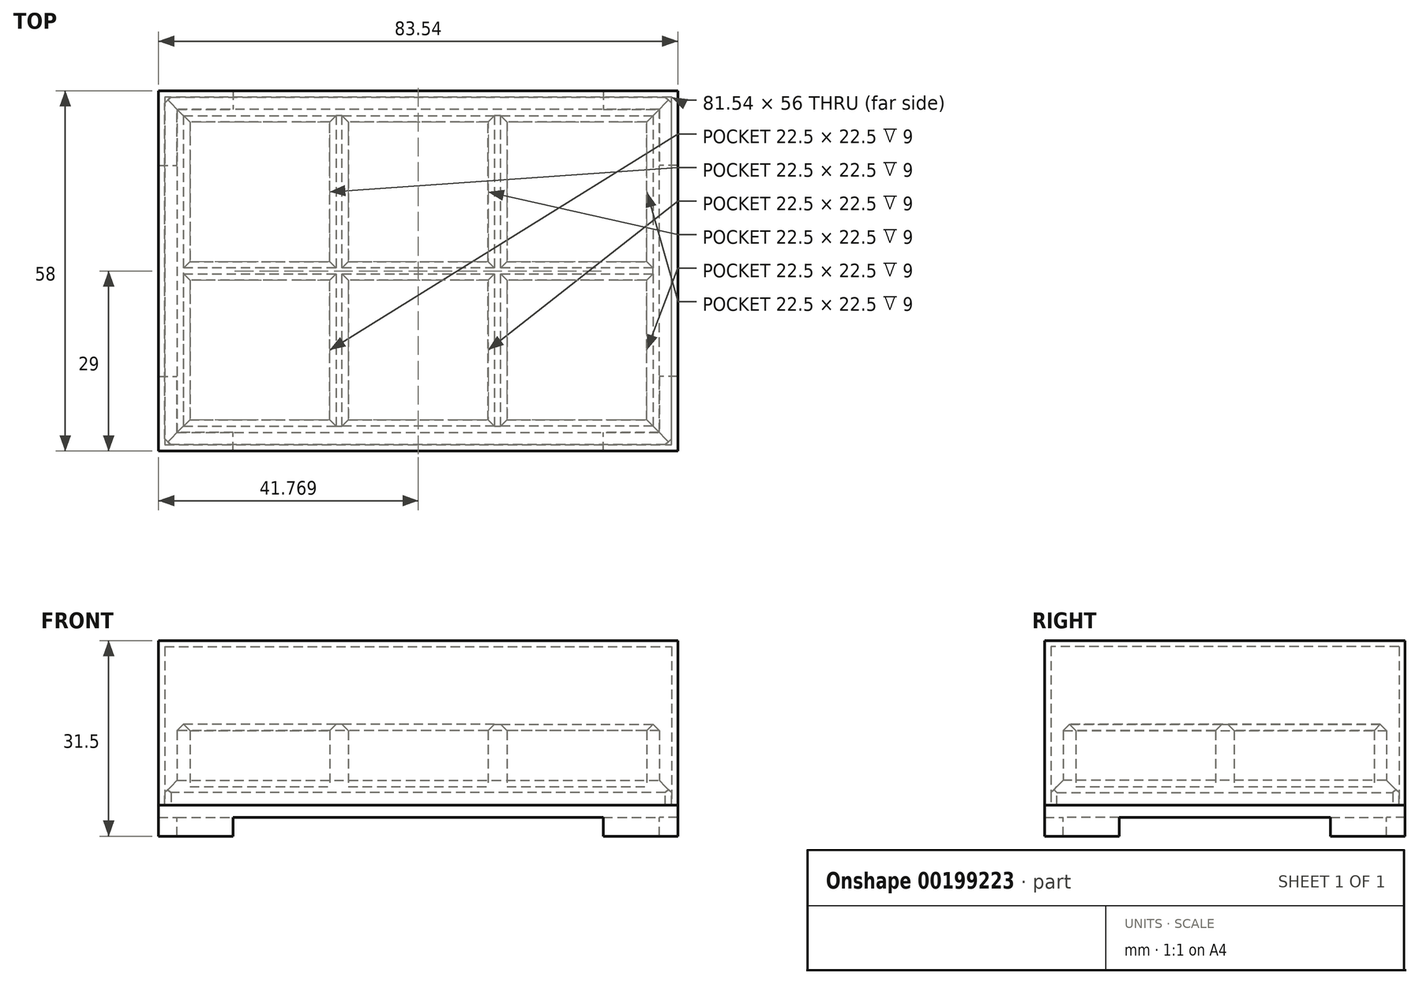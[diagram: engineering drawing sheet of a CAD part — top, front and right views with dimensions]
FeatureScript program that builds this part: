
annotation { "Feature Type Name" : "Feature", "Feature Type Description" : "" }
export const myFeature = defineFeature(function(context is Context, id is Id, definition is map)
    precondition{}
    {
        {
            var Q0;
            Q0=qCreatedBy(makeId("Top.planeOp"),FACE);
            var sketch = newSketch(context, id + "F0", { "sketchPlane" : qUnion([Q0])});
            skLineSegment(sketch, "E0.bottom", {"start": v(0, 0) * mm, "end": v(22.5, 0) * mm});
            skLineSegment(sketch, "E0.top", {"start": v(0, 22.5) * mm, "end": v(22.5, 22.5) * mm});
            skLineSegment(sketch, "E0.left", {"start": v(0, 0) * mm, "end": v(0, 22.5) * mm});
            skLineSegment(sketch, "E0.right", {"start": v(22.5, 0) * mm, "end": v(22.5, 22.5) * mm});
            skLineSegment(sketch, "E1.0.1.0", {"start": v(0, 48) * mm, "end": v(22.5, 48) * mm});
            skLineSegment(sketch, "E1.0.1.1", {"start": v(0, 25.5) * mm, "end": v(0, 48) * mm});
            skLineSegment(sketch, "E1.0.1.2", {"start": v(0, 25.5) * mm, "end": v(22.5, 25.5) * mm});
            skLineSegment(sketch, "E1.0.1.3", {"start": v(22.5, 25.5) * mm, "end": v(22.5, 48) * mm});
            skLineSegment(sketch, "E1.1.0.0", {"start": v(25.5, 22.5) * mm, "end": v(48, 22.5) * mm});
            skLineSegment(sketch, "E1.1.0.1", {"start": v(25.5, 0) * mm, "end": v(25.5, 22.5) * mm});
            skLineSegment(sketch, "E1.1.0.2", {"start": v(25.5, 0) * mm, "end": v(48, 0) * mm});
            skLineSegment(sketch, "E1.1.0.3", {"start": v(48, 0) * mm, "end": v(48, 22.5) * mm});
            skLineSegment(sketch, "E1.1.1.0", {"start": v(25.5, 48) * mm, "end": v(48, 48) * mm});
            skLineSegment(sketch, "E1.1.1.1", {"start": v(25.5, 25.5) * mm, "end": v(25.5, 48) * mm});
            skLineSegment(sketch, "E1.1.1.2", {"start": v(25.5, 25.5) * mm, "end": v(48, 25.5) * mm});
            skLineSegment(sketch, "E1.1.1.3", {"start": v(48, 25.5) * mm, "end": v(48, 48) * mm});
            skLineSegment(sketch, "E1.2.0.0", {"start": v(51, 22.5) * mm, "end": v(73.5, 22.5) * mm});
            skLineSegment(sketch, "E1.2.0.1", {"start": v(51, 0) * mm, "end": v(51, 22.5) * mm});
            skLineSegment(sketch, "E1.2.0.2", {"start": v(51, 0) * mm, "end": v(73.5, 0) * mm});
            skLineSegment(sketch, "E1.2.0.3", {"start": v(73.5, 0) * mm, "end": v(73.5, 22.5) * mm});
            skLineSegment(sketch, "E1.2.1.0", {"start": v(51, 48) * mm, "end": v(73.5, 48) * mm});
            skLineSegment(sketch, "E1.2.1.1", {"start": v(51, 25.5) * mm, "end": v(51, 48) * mm});
            skLineSegment(sketch, "E1.2.1.2", {"start": v(51, 25.5) * mm, "end": v(73.5, 25.5) * mm});
            skLineSegment(sketch, "E1.2.1.3", {"start": v(73.5, 25.5) * mm, "end": v(73.5, 48) * mm});
            skLineSegment(sketch, "E1.direction1", {"start": v(0, 22.5) * mm, "end": v(25.5, 22.5) * mm, "construction": true});
            skLineSegment(sketch, "E1.direction2", {"start": v(0, 22.5) * mm, "end": v(0, 48) * mm, "construction": true});
            skLineSegment(sketch, "E2.bottom", {"start": v(-2.04, -2) * mm, "end": v(75.5, -2) * mm});
            skLineSegment(sketch, "E2.top", {"start": v(-2.04, 50) * mm, "end": v(75.5, 50) * mm});
            skLineSegment(sketch, "E2.left", {"start": v(-2.04, -2) * mm, "end": v(-2.04, 50) * mm});
            skLineSegment(sketch, "E2.right", {"start": v(75.5, -2) * mm, "end": v(75.5, 50) * mm});
            skSolve(sketch);
        }
        {
            var Q0;
            Q0 = qSketchRegion(id + "F0", true);
            extrude(context, id + "F1", {"entities" : qUnion([Q0]), "depth" : 10 * mm});
        }
        {
            var Q0;
            Q0=makeQuery(id+"F1.opExtrude","CAP_FACE",FACE,{"disambiguationData":[OSD([sQuery(id+"F0.wireOp",EDGE,"E0.bottom"),sQuery(id+"F0.wireOp",EDGE,"E0.top"),sQuery(id+"F0.wireOp",EDGE,"E0.left"),sQuery(id+"F0.wireOp",EDGE,"E0.right"),sQuery(id+"F0.wireOp",EDGE,"E1.0.1.0"),sQuery(id+"F0.wireOp",EDGE,"E1.0.1.1"),sQuery(id+"F0.wireOp",EDGE,"E1.0.1.2"),sQuery(id+"F0.wireOp",EDGE,"E1.0.1.3"),sQuery(id+"F0.wireOp",EDGE,"E1.1.0.0"),sQuery(id+"F0.wireOp",EDGE,"E1.1.0.1"),sQuery(id+"F0.wireOp",EDGE,"E1.1.0.2"),sQuery(id+"F0.wireOp",EDGE,"E1.1.0.3"),sQuery(id+"F0.wireOp",EDGE,"E1.1.1.0"),sQuery(id+"F0.wireOp",EDGE,"E1.1.1.1"),sQuery(id+"F0.wireOp",EDGE,"E1.1.1.2"),sQuery(id+"F0.wireOp",EDGE,"E1.1.1.3"),sQuery(id+"F0.wireOp",EDGE,"E1.2.0.0"),sQuery(id+"F0.wireOp",EDGE,"E1.2.0.1"),sQuery(id+"F0.wireOp",EDGE,"E1.2.0.2"),sQuery(id+"F0.wireOp",EDGE,"E1.2.0.3"),sQuery(id+"F0.wireOp",EDGE,"E1.2.1.0"),sQuery(id+"F0.wireOp",EDGE,"E1.2.1.1"),sQuery(id+"F0.wireOp",EDGE,"E1.2.1.2"),sQuery(id+"F0.wireOp",EDGE,"E1.2.1.3"),sQuery(id+"F0.wireOp",EDGE,"E2.bottom"),sQuery(id+"F0.wireOp",EDGE,"E2.top"),sQuery(id+"F0.wireOp",EDGE,"E2.left"),sQuery(id+"F0.wireOp",EDGE,"E2.right")])],"isStart":true});
            var sketch = newSketch(context, id + "F2", { "sketchPlane" : qUnion([Q0])});
            skLineSegment(sketch, "E3.0", {"start": v(-4.04, 4) * mm, "end": v(-4.04, -52) * mm});
            skLineSegment(sketch, "E3.1", {"start": v(-4.04, 4) * mm, "end": v(77.5, 4) * mm});
            skLineSegment(sketch, "E3.2", {"start": v(77.5, 4) * mm, "end": v(77.5, -52) * mm});
            skLineSegment(sketch, "E3.3", {"start": v(-4.04, -52) * mm, "end": v(77.5, -52) * mm});
            skSolve(sketch);
        }
        {
            var Q0;
            Q0 = qSketchRegion(id + "F2", true);
            extrude(context, id + "F3", {"entities" : qUnion([Q0]), "operationType" : NewBodyOperationType.ADD, "depth" : 3 * mm});
        }
        {
            var Q0;
            Q0=makeQuery(id+"F3.opExtrude","CAP_FACE",FACE,{"disambiguationData":[OSD([sQuery(id+"F2.wireOp",EDGE,"E3.0"),sQuery(id+"F2.wireOp",EDGE,"E3.1"),sQuery(id+"F2.wireOp",EDGE,"E3.2"),sQuery(id+"F2.wireOp",EDGE,"E3.3")])],"isStart":false});
            var sketch = newSketch(context, id + "F4", { "sketchPlane" : qUnion([Q0])});
            skLineSegment(sketch, "E4.0", {"start": v(78.5, 5) * mm, "end": v(-5.04, 5) * mm});
            skLineSegment(sketch, "E4.1", {"start": v(78.5, -53) * mm, "end": v(78.5, 5) * mm});
            skLineSegment(sketch, "E4.2", {"start": v(-5.04, -53) * mm, "end": v(78.5, -53) * mm});
            skLineSegment(sketch, "E4.3", {"start": v(-5.04, 5) * mm, "end": v(-5.04, -53) * mm});
            skSolve(sketch);
        }
        {
            var Q0;
            Q0 = qSketchRegion(id + "F4", true);
            extrude(context, id + "F5", {"entities" : qUnion([Q0]), "operationType" : NewBodyOperationType.ADD, "depth" : 2 * mm});
        }
        {
            var Q0;
            Q0=makeQuery(id+"F3.opExtrude","CAP_EDGE",EDGE,{"disambiguationData":[OSD([sQuery(id+"F2.wireOp",EDGE,"E3.2")])],"isStart":true});
            var Q1;
            Q1=makeQuery(id+"F3.opExtrude","CAP_EDGE",EDGE,{"disambiguationData":[OSD([sQuery(id+"F2.wireOp",EDGE,"E3.3")])],"isStart":true});
            var Q2;
            Q2=makeQuery(id+"F3.opExtrude","CAP_EDGE",EDGE,{"disambiguationData":[OSD([sQuery(id+"F2.wireOp",EDGE,"E3.0")])],"isStart":true});
            var Q3;
            Q3=makeQuery(id+"F3.opExtrude","CAP_EDGE",EDGE,{"disambiguationData":[OSD([sQuery(id+"F2.wireOp",EDGE,"E3.1")])],"isStart":true});
            chamfer(context, id + "F6", {"entities" : qUnion([Q0, Q1, Q2, Q3]), "width" : 1 * mm, "tangentPropagation" : true});
        }
        {
            var Q0;
            Q0=makeQuery(id+"F1.opExtrude","CAP_EDGE",EDGE,{"disambiguationData":[OSD([sQuery(id+"F0.wireOp",EDGE,"E0.right")])],"isStart":false});
            var Q1;
            Q1=makeQuery(id+"F1.opExtrude","CAP_EDGE",EDGE,{"disambiguationData":[OSD([sQuery(id+"F0.wireOp",EDGE,"E0.bottom")])],"isStart":false});
            var Q2;
            Q2=makeQuery(id+"F1.opExtrude","CAP_EDGE",EDGE,{"disambiguationData":[OSD([sQuery(id+"F0.wireOp",EDGE,"E0.left")])],"isStart":false});
            var Q3;
            Q3=makeQuery(id+"F1.opExtrude","CAP_EDGE",EDGE,{"disambiguationData":[OSD([sQuery(id+"F0.wireOp",EDGE,"E0.top")])],"isStart":false});
            var Q4;
            Q4=makeQuery(id+"F1.opExtrude","CAP_EDGE",EDGE,{"disambiguationData":[OSD([sQuery(id+"F0.wireOp",EDGE,"E1.1.0.3")])],"isStart":false});
            var Q5;
            Q5=makeQuery(id+"F1.opExtrude","CAP_EDGE",EDGE,{"disambiguationData":[OSD([sQuery(id+"F0.wireOp",EDGE,"E1.1.0.2")])],"isStart":false});
            var Q6;
            Q6=makeQuery(id+"F1.opExtrude","CAP_EDGE",EDGE,{"disambiguationData":[OSD([sQuery(id+"F0.wireOp",EDGE,"E1.1.0.1")])],"isStart":false});
            var Q7;
            Q7=makeQuery(id+"F1.opExtrude","CAP_EDGE",EDGE,{"disambiguationData":[OSD([sQuery(id+"F0.wireOp",EDGE,"E1.1.0.0")])],"isStart":false});
            var Q8;
            Q8=makeQuery(id+"F1.opExtrude","CAP_EDGE",EDGE,{"disambiguationData":[OSD([sQuery(id+"F0.wireOp",EDGE,"E1.2.0.0")])],"isStart":false});
            var Q9;
            Q9=makeQuery(id+"F1.opExtrude","CAP_EDGE",EDGE,{"disambiguationData":[OSD([sQuery(id+"F0.wireOp",EDGE,"E1.2.0.3")])],"isStart":false});
            var Q10;
            Q10=makeQuery(id+"F1.opExtrude","CAP_EDGE",EDGE,{"disambiguationData":[OSD([sQuery(id+"F0.wireOp",EDGE,"E1.2.0.2")])],"isStart":false});
            var Q11;
            Q11=makeQuery(id+"F1.opExtrude","CAP_EDGE",EDGE,{"disambiguationData":[OSD([sQuery(id+"F0.wireOp",EDGE,"E1.2.0.1")])],"isStart":false});
            var Q12;
            Q12=makeQuery(id+"F1.opExtrude","CAP_EDGE",EDGE,{"disambiguationData":[OSD([sQuery(id+"F0.wireOp",EDGE,"E1.2.1.2")])],"isStart":false});
            var Q13;
            Q13=makeQuery(id+"F1.opExtrude","CAP_EDGE",EDGE,{"disambiguationData":[OSD([sQuery(id+"F0.wireOp",EDGE,"E1.2.1.3")])],"isStart":false});
            var Q14;
            Q14=makeQuery(id+"F1.opExtrude","CAP_EDGE",EDGE,{"disambiguationData":[OSD([sQuery(id+"F0.wireOp",EDGE,"E1.2.1.0")])],"isStart":false});
            var Q15;
            Q15=makeQuery(id+"F1.opExtrude","CAP_EDGE",EDGE,{"disambiguationData":[OSD([sQuery(id+"F0.wireOp",EDGE,"E1.2.1.1")])],"isStart":false});
            var Q16;
            Q16=makeQuery(id+"F1.opExtrude","CAP_EDGE",EDGE,{"disambiguationData":[OSD([sQuery(id+"F0.wireOp",EDGE,"E1.1.1.2")])],"isStart":false});
            var Q17;
            Q17=makeQuery(id+"F1.opExtrude","CAP_EDGE",EDGE,{"disambiguationData":[OSD([sQuery(id+"F0.wireOp",EDGE,"E1.1.1.3")])],"isStart":false});
            var Q18;
            Q18=makeQuery(id+"F1.opExtrude","CAP_EDGE",EDGE,{"disambiguationData":[OSD([sQuery(id+"F0.wireOp",EDGE,"E1.1.1.0")])],"isStart":false});
            var Q19;
            Q19=makeQuery(id+"F1.opExtrude","CAP_EDGE",EDGE,{"disambiguationData":[OSD([sQuery(id+"F0.wireOp",EDGE,"E1.0.1.3")])],"isStart":false});
            var Q20;
            Q20=makeQuery(id+"F1.opExtrude","CAP_EDGE",EDGE,{"disambiguationData":[OSD([sQuery(id+"F0.wireOp",EDGE,"E1.0.1.2")])],"isStart":false});
            var Q21;
            Q21=makeQuery(id+"F1.opExtrude","CAP_EDGE",EDGE,{"disambiguationData":[OSD([sQuery(id+"F0.wireOp",EDGE,"E1.0.1.1")])],"isStart":false});
            var Q22;
            Q22=makeQuery(id+"F1.opExtrude","CAP_FACE",FACE,{"disambiguationData":[OSD([sQuery(id+"F0.wireOp",EDGE,"E0.bottom"),sQuery(id+"F0.wireOp",EDGE,"E0.top"),sQuery(id+"F0.wireOp",EDGE,"E0.left"),sQuery(id+"F0.wireOp",EDGE,"E0.right"),sQuery(id+"F0.wireOp",EDGE,"E1.0.1.0"),sQuery(id+"F0.wireOp",EDGE,"E1.0.1.1"),sQuery(id+"F0.wireOp",EDGE,"E1.0.1.2"),sQuery(id+"F0.wireOp",EDGE,"E1.0.1.3"),sQuery(id+"F0.wireOp",EDGE,"E1.1.0.0"),sQuery(id+"F0.wireOp",EDGE,"E1.1.0.1"),sQuery(id+"F0.wireOp",EDGE,"E1.1.0.2"),sQuery(id+"F0.wireOp",EDGE,"E1.1.0.3"),sQuery(id+"F0.wireOp",EDGE,"E1.1.1.0"),sQuery(id+"F0.wireOp",EDGE,"E1.1.1.1"),sQuery(id+"F0.wireOp",EDGE,"E1.1.1.2"),sQuery(id+"F0.wireOp",EDGE,"E1.1.1.3"),sQuery(id+"F0.wireOp",EDGE,"E1.2.0.0"),sQuery(id+"F0.wireOp",EDGE,"E1.2.0.1"),sQuery(id+"F0.wireOp",EDGE,"E1.2.0.2"),sQuery(id+"F0.wireOp",EDGE,"E1.2.0.3"),sQuery(id+"F0.wireOp",EDGE,"E1.2.1.0"),sQuery(id+"F0.wireOp",EDGE,"E1.2.1.1"),sQuery(id+"F0.wireOp",EDGE,"E1.2.1.2"),sQuery(id+"F0.wireOp",EDGE,"E1.2.1.3"),sQuery(id+"F0.wireOp",EDGE,"E2.bottom"),sQuery(id+"F0.wireOp",EDGE,"E2.top"),sQuery(id+"F0.wireOp",EDGE,"E2.left"),sQuery(id+"F0.wireOp",EDGE,"E2.right")])],"isStart":false});
            var Q23;
            Q23=makeQuery(id+"F1.opExtrude","CAP_EDGE",EDGE,{"disambiguationData":[OSD([sQuery(id+"F0.wireOp",EDGE,"E2.top")])],"isStart":true});
            var Q24;
            Q24=makeQuery(id+"F1.opExtrude","CAP_EDGE",EDGE,{"disambiguationData":[OSD([sQuery(id+"F0.wireOp",EDGE,"E2.left")])],"isStart":true});
            var Q25;
            Q25=makeQuery(id+"F1.opExtrude","CAP_EDGE",EDGE,{"disambiguationData":[OSD([sQuery(id+"F0.wireOp",EDGE,"E2.right")])],"isStart":true});
            var Q26;
            Q26=makeQuery(id+"F1.opExtrude","CAP_EDGE",EDGE,{"disambiguationData":[OSD([sQuery(id+"F0.wireOp",EDGE,"E2.bottom")])],"isStart":true});
            var Q27;
            Q27=makeQuery(id+"F3.opExtrude","SWEPT_EDGE",EDGE,{"disambiguationData":[OSD([sQuery(id+"F2.wireOp",EDGE,"E3.0"),sQuery(id+"F2.wireOp",EDGE,"E3.1")])]});
            var Q28;
            Q28=makeQuery(id+"F3.opExtrude","SWEPT_EDGE",EDGE,{"disambiguationData":[OSD([sQuery(id+"F2.wireOp",EDGE,"E3.0"),sQuery(id+"F2.wireOp",EDGE,"E3.3")])]});
            var Q29;
            Q29=makeQuery(id+"F3.opExtrude","SWEPT_EDGE",EDGE,{"disambiguationData":[OSD([sQuery(id+"F2.wireOp",EDGE,"E3.2"),sQuery(id+"F2.wireOp",EDGE,"E3.3")])]});
            var Q30;
            Q30=makeQuery(id+"F3.opExtrude","SWEPT_EDGE",EDGE,{"disambiguationData":[OSD([sQuery(id+"F2.wireOp",EDGE,"E3.1"),sQuery(id+"F2.wireOp",EDGE,"E3.2")])]});
            chamfer(context, id + "F7", {"entities" : qUnion([Q0, Q1, Q2, Q3, Q4, Q5, Q6, Q7, Q8, Q9, Q10, Q11, Q12, Q13, Q14, Q15, Q16, Q17, Q18, Q19, Q20, Q21, Q22, Q23, Q24, Q25, Q26, Q27, Q28, Q29, Q30]), "width" : 1 * mm, "tangentPropagation" : true});
        }
        {
            var Q0;
            Q0=makeQuery(id+"F5.opExtrude","CAP_FACE",FACE,{"disambiguationData":[OSD([sQuery(id+"F4.wireOp",EDGE,"E4.0"),sQuery(id+"F4.wireOp",EDGE,"E4.1"),sQuery(id+"F4.wireOp",EDGE,"E4.2"),sQuery(id+"F4.wireOp",EDGE,"E4.3")])],"isStart":false});
            var sketch = newSketch(context, id + "F8", { "sketchPlane" : qUnion([Q0])});
            skLineSegment(sketch, "E5.0.0", {"start": v(78.5, -53) * mm, "end": v(78.5, 5) * mm});
            skLineSegment(sketch, "E5.0.1", {"start": v(78.5, 5) * mm, "end": v(-5.04, 5) * mm});
            skLineSegment(sketch, "E5.0.2", {"start": v(-5.04, 5) * mm, "end": v(-5.04, -53) * mm});
            skLineSegment(sketch, "E5.0.3", {"start": v(-5.04, -53) * mm, "end": v(78.5, -53) * mm});
            skLineSegment(sketch, "E6.0", {"start": v(75.5, -50) * mm, "end": v(75.5, 2) * mm});
            skLineSegment(sketch, "E6.1", {"start": v(-2.04, -50) * mm, "end": v(75.5, -50) * mm});
            skLineSegment(sketch, "E6.2", {"start": v(-2.04, 2) * mm, "end": v(-2.04, -50) * mm});
            skLineSegment(sketch, "E6.3", {"start": v(75.5, 2) * mm, "end": v(-2.04, 2) * mm});
            skLineSegment(sketch, "E7", {"start": v(66.5, 5) * mm, "end": v(66.5, 2) * mm});
            skLineSegment(sketch, "E8", {"start": v(78.5, -7) * mm, "end": v(75.5, -7) * mm});
            skLineSegment(sketch, "E9", {"start": v(75.5, -24) * mm, "end": v(-2.04, -24) * mm, "construction": true});
            skLineSegment(sketch, "E10", {"start": v(36.73, 2) * mm, "end": v(36.73, -50) * mm, "construction": true});
            skLineSegment(sketch, "E11.MirrorCS", {"start": v(66.5, -53) * mm, "end": v(66.5, -50) * mm});
            skLineSegment(sketch, "E12.MirrorCS", {"start": v(78.5, -41) * mm, "end": v(75.5, -41) * mm});
            skLineSegment(sketch, "E13.MirrorCS", {"start": v(6.96, 5) * mm, "end": v(6.96, 2) * mm});
            skLineSegment(sketch, "E14.MirrorCS", {"start": v(-5.04, -7) * mm, "end": v(-2.04, -7) * mm});
            skLineSegment(sketch, "E15.MirrorCS", {"start": v(-5.04, -41) * mm, "end": v(-2.04, -41) * mm});
            skLineSegment(sketch, "E16.MirrorCS", {"start": v(6.96, -53) * mm, "end": v(6.96, -50) * mm});
            skSolve(sketch);
        }
        {
            var Q0;
            {var subQ7=sQuery(id+"F8.wireOp",EDGE,"E7");Q0=makeQuery(id+"F8.imprint","IMPRINT",FACE,{"disambiguationData":[TD([[makeQuery(id+"F8.imprint","IMPRINT",EDGE,{"derivedFrom":subQ7}),1.0]])]});}
            var Q1;
            {var subQ3=sQuery(id+"F8.wireOp",EDGE,"E11.MirrorCS");Q1=makeQuery(id+"F8.imprint","IMPRINT",FACE,{"disambiguationData":[TD([[makeQuery(id+"F8.imprint","IMPRINT",EDGE,{"derivedFrom":subQ3}),-1.0]])]});}
            var Q2;
            {var subQ3=sQuery(id+"F8.wireOp",EDGE,"E15.MirrorCS");Q2=makeQuery(id+"F8.imprint","IMPRINT",FACE,{"disambiguationData":[TD([[makeQuery(id+"F8.imprint","IMPRINT",EDGE,{"derivedFrom":subQ3}),-1.0]])]});}
            var Q3;
            {var subQ3=sQuery(id+"F8.wireOp",EDGE,"E13.MirrorCS");Q3=makeQuery(id+"F8.imprint","IMPRINT",FACE,{"disambiguationData":[TD([[makeQuery(id+"F8.imprint","IMPRINT",EDGE,{"derivedFrom":subQ3}),-1.0]])]});}
            extrude(context, id + "F9", {"entities" : qUnion([Q0, Q1, Q2, Q3]), "operationType" : NewBodyOperationType.ADD, "depth" : 3 * mm});
        }
        {
            var Q0;
            Q0=makeQuery(id+"F5.opExtrude","CAP_FACE",FACE,{"disambiguationData":[OSD([sQuery(id+"F4.wireOp",EDGE,"E4.0"),sQuery(id+"F4.wireOp",EDGE,"E4.1"),sQuery(id+"F4.wireOp",EDGE,"E4.2"),sQuery(id+"F4.wireOp",EDGE,"E4.3")])],"isStart":true});
            var sketch = newSketch(context, id + "F10", { "sketchPlane" : qUnion([Q0])});
            skLineSegment(sketch, "E17.0", {"start": v(-5.04, 53) * mm, "end": v(78.5, 53) * mm});
            skLineSegment(sketch, "E18.0", {"start": v(-5.04, -5) * mm, "end": v(-5.04, 53) * mm});
            skLineSegment(sketch, "E19.0", {"start": v(78.5, 53) * mm, "end": v(78.5, -5) * mm});
            skLineSegment(sketch, "E20.0", {"start": v(78.5, -5) * mm, "end": v(-5.04, -5) * mm});
            skLineSegment(sketch, "E21", {"start": v(-4.04, -4) * mm, "end": v(77.5, -4) * mm});
            skLineSegment(sketch, "E22", {"start": v(77.5, -4) * mm, "end": v(77.5, 52) * mm});
            skLineSegment(sketch, "E23", {"start": v(77.5, 52) * mm, "end": v(-4.04, 52) * mm});
            skLineSegment(sketch, "E24", {"start": v(-4.04, 52) * mm, "end": v(-4.04, -4) * mm});
            skSolve(sketch);
        }
        {
            var Q0;
            Q0 = qSketchRegion(id + "F10", true);
            extrude(context, id + "F11", {"entities" : qUnion([Q0]), "depth" : 25.5 * mm});
        }
        {
            var Q0;
            Q0=makeQuery(id+"F11.opExtrude","CAP_FACE",FACE,{"disambiguationData":[OSD([sQuery(id+"F10.wireOp",EDGE,"E17.0"),sQuery(id+"F10.wireOp",EDGE,"E18.0"),sQuery(id+"F10.wireOp",EDGE,"E19.0"),sQuery(id+"F10.wireOp",EDGE,"E20.0"),sQuery(id+"F10.wireOp",EDGE,"E21"),sQuery(id+"F10.wireOp",EDGE,"E22"),sQuery(id+"F10.wireOp",EDGE,"E23"),sQuery(id+"F10.wireOp",EDGE,"E24")])],"isStart":false});
            var sketch = newSketch(context, id + "F12", { "sketchPlane" : qUnion([Q0])});
            skLineSegment(sketch, "E25.bottom", {"start": v(-5.04, 53) * mm, "end": v(78.5, 53) * mm});
            skLineSegment(sketch, "E25.top", {"start": v(-5.04, -5) * mm, "end": v(78.5, -5) * mm});
            skLineSegment(sketch, "E25.left", {"start": v(-5.04, 53) * mm, "end": v(-5.04, -5) * mm});
            skLineSegment(sketch, "E25.right", {"start": v(78.5, 53) * mm, "end": v(78.5, -5) * mm});
            skSolve(sketch);
        }
        {
            var Q0;
            Q0 = qSketchRegion(id + "F12", true);
            extrude(context, id + "F13", {"entities" : qUnion([Q0]), "operationType" : NewBodyOperationType.ADD, "depth" : 1 * mm});
        }
    });
